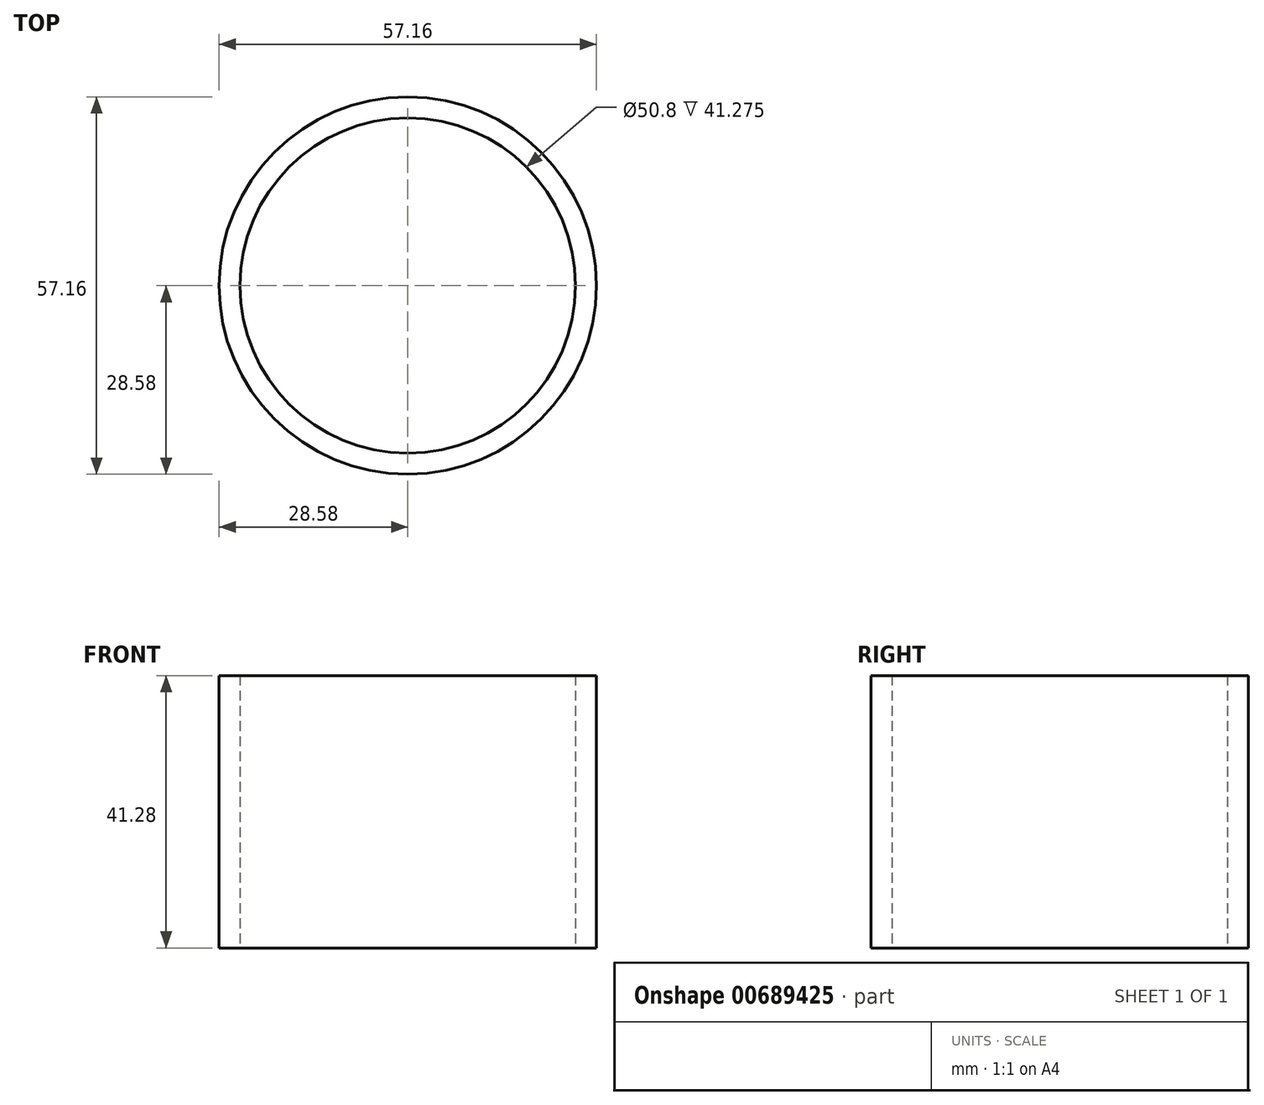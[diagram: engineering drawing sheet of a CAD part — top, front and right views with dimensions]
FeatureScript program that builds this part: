
annotation { "Feature Type Name" : "Feature", "Feature Type Description" : "" }
export const myFeature = defineFeature(function(context is Context, id is Id, definition is map)
    precondition{}
    {
        {
            var Q0;
            Q0=qCreatedBy(makeId("Top.planeOp"),FACE);
            var sketch = newSketch(context, id + "F0", { "sketchPlane" : qUnion([Q0])});
            skCircle(sketch, "E0", {"center": v(0, 0) * mm, "radius": 28.58 * mm});
            skCircle(sketch, "E1", {"center": v(0, 0) * mm, "radius": 25.4 * mm});
            skSolve(sketch);
        }
        {
            var Q0;
            Q0=makeQuery(id+"F0.imprint","IMPRINT",FACE,{"disambiguationData":[TD([[makeQuery(id+"F0.imprint","IMPRINT",EDGE,{"derivedFrom":sQuery(id+"F0.wireOp",EDGE,"E0")}),1.0]])]});
            extrude(context, id + "F1", {"entities" : qUnion([Q0]), "depth" : 41.27 * mm, "offsetDistance" : 25.4 * mm});
        }
    });
